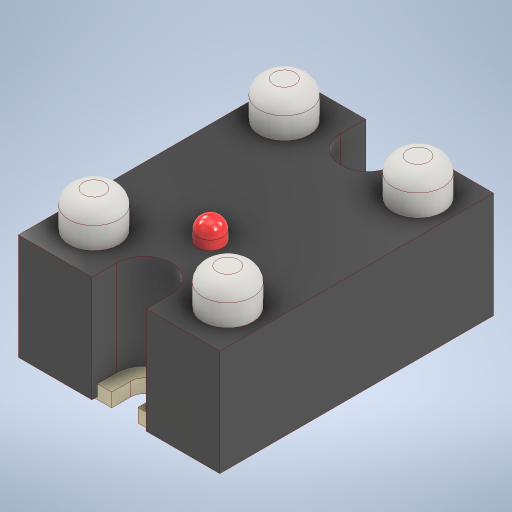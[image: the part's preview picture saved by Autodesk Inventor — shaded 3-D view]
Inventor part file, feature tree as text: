
AUTODESK INVENTOR PART (.ipt)
format: ipt  version: 2023 (Build 270158030, 158C)  size: 368,128 bytes
history: native  units: mm
features: other x4, extrude x4, sketch x4, fillet x2, plane x1, projected_geometry x1
ambient origin geometry x8: Origin, YZ Plane, XZ Plane, XY Plane, X Axis, Y Axis, Z Axis, Center Point
bodies: Body1 (feature_tree), Body2 (feature_tree), Body3 (feature_tree), Body4 (feature_tree)
feature tree (16):
  other  "plate"
  extrude  "Extrusion1"  Depth=26.2mm
  plane  "Work Plane1"
  extrude  "Extrusion2"  Depth=1.9mm TaperAngle=0.0deg
  extrude  "Extrusion3"  Depth=3.64mm
  fillet  "Fillet1"  Radius=3.64mm
  extrude  "Extrusion4"  Depth=36.2mm
  fillet  "Fillet2"  Radius=18.1mm
  sketch  "Sketch1"  dims[d0=36.2mm d1=26.2mm d2=13.1mm]
  sketch  "Sketch2"  dims[d3=18.1mm d4=1.9mm d5=0.0mm]
  projected_geometry  "Projected Loop1"
  other  "case"
  sketch  "Sketch3"  dims[d6=3.64mm d7=2.65mm d8=3.64mm]
  other  "screw-terminals"
  sketch  "Sketch4"  dims[d9=2.65mm d10=36.2mm d11=18.1mm d12=2.65mm d13=-0.4mm d14=0.8mm d15=7.5mm d17=0.8mm d18=0.8mm d20=0.8mm d21=3.75mm d23=7.5mm d24=14.66mm d25=0.0mm d26=4.66mm d27=5.76mm d28=6.94mm d29=4.66mm d30=5.76mm d31=5.0mm d32=0.0mm d33=2.0mm d34=3.5mm d35=12.6mm d36=3.0mm d37=0.0mm d38=1.75mm]
  other  "led"
